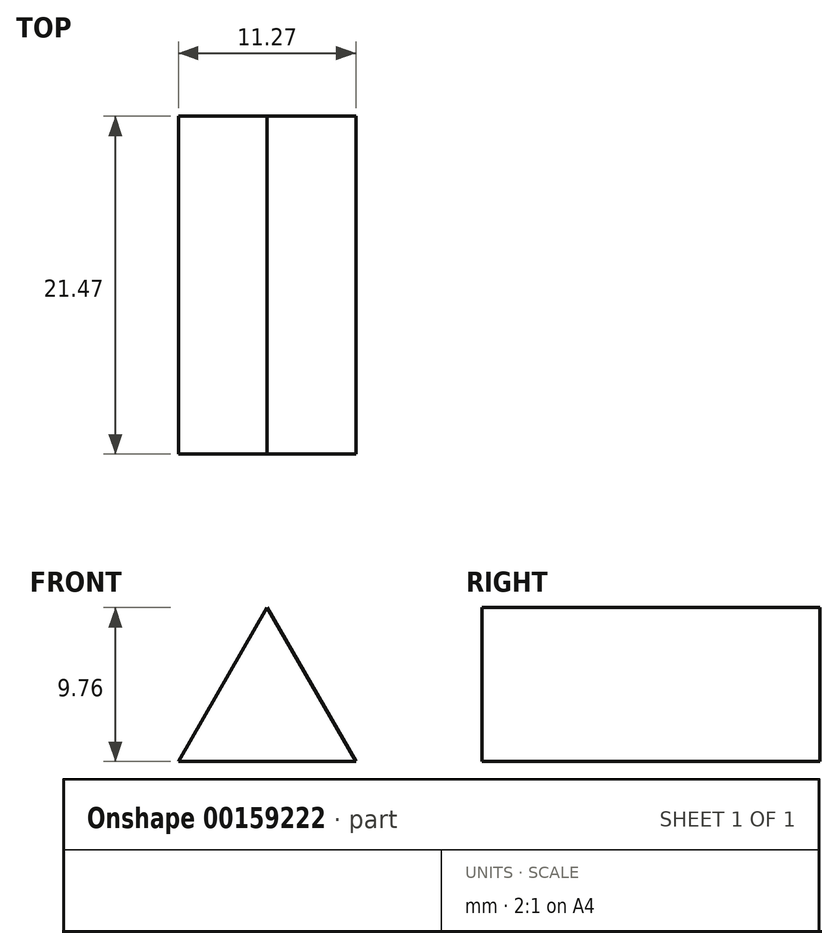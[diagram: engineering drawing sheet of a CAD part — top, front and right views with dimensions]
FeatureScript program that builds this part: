
annotation { "Feature Type Name" : "Feature", "Feature Type Description" : "" }
export const myFeature = defineFeature(function(context is Context, id is Id, definition is map)
    precondition{}
    {
        {
            var Q0;
            Q0=qCreatedBy(makeId("Front.planeOp"),FACE);
            var sketch = newSketch(context, id + "F0", { "sketchPlane" : qUnion([Q0])});
            skLineSegment(sketch, "E0.0", {"start": v(-34.58, 43.01) * mm, "end": v(-45.85, 43.01) * mm});
            skLineSegment(sketch, "E0.1", {"start": v(-45.85, 43.01) * mm, "end": v(-40.22, 52.77) * mm});
            skLineSegment(sketch, "E0.2", {"start": v(-40.22, 52.77) * mm, "end": v(-34.58, 43.01) * mm});
            skPoint(sketch, "E0.0.midPoint", {"position": v(-40.22, 43.01) * mm});
            skPoint(sketch, "E0.cCircle.center.orphan", {"position": v(-40.22, 46.27) * mm});
            skSolve(sketch);
        }
        {
            var Q0;
            Q0 = qSketchRegion(id + "F0", true);
            extrude(context, id + "F1", {"entities" : qUnion([Q0]), "oppositeDirection" : true, "depth" : 21.47 * mm});
        }
    });
